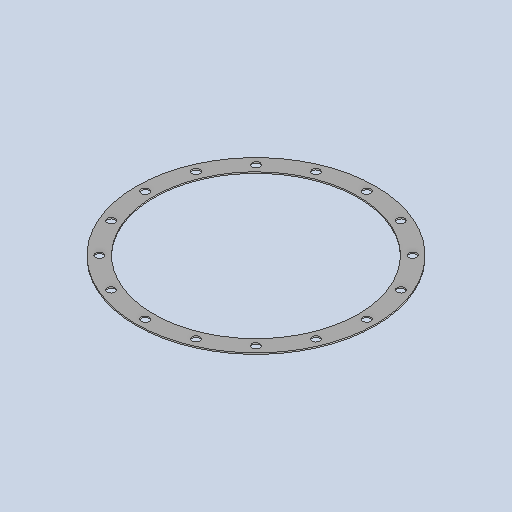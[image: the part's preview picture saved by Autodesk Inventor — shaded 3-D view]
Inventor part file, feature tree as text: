
AUTODESK INVENTOR PART (.ipt)
format: ipt  version: 2024.2 (Build 282272000, 272)  size: 128,000 bytes
history: native  units: mm
features: sketch x2, sheet_metal_op x1, extrude x1, pattern_circular x1, other x1, projected_geometry x1
ambient origin geometry x8: Origin, YZ Plane, XZ Plane, XY Plane, X Axis, Y Axis, Z Axis, Center Point
bodies: Solid1 (feature_tree)
feature tree (7):
  sheet_metal_op  "Face1"
  extrude  "Extrusion1"  Depth=3.0mm
  pattern_circular  "Circular Pattern1"  Count=16 Angle=360.0deg
  sketch  "Sketch1"  dims[d2=3.0mm d3=18.0mm]
  other  "Plate1"
  sketch  "Sketch2"  dims[d4=0.0mm d5=0.0mm d6=160.0mm d7=360.0deg d9=510.0mm d10=40.0mm]
  projected_geometry  "Projected Loop1"
